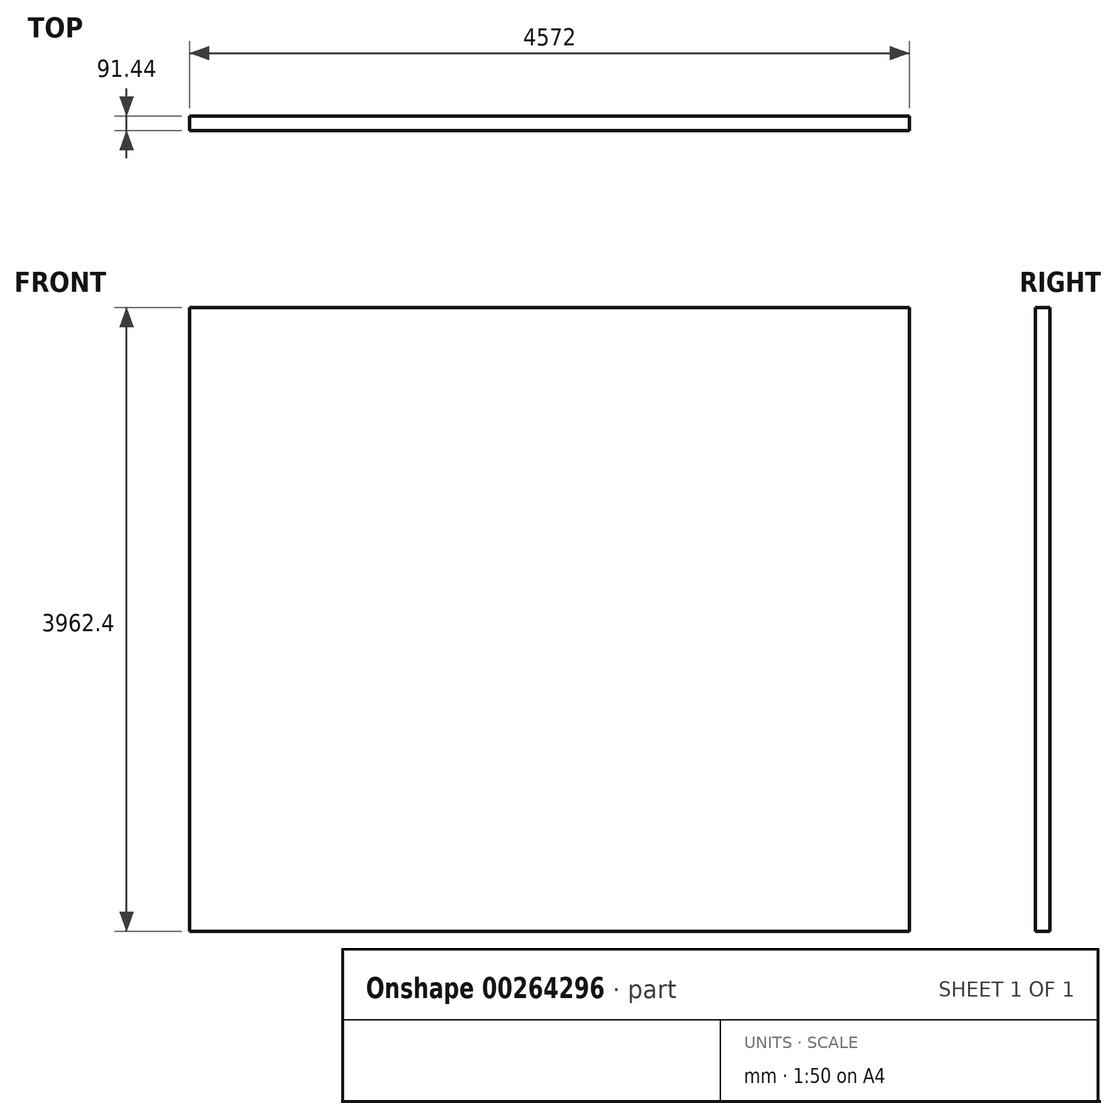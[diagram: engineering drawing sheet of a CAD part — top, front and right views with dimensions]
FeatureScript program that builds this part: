
annotation { "Feature Type Name" : "Feature", "Feature Type Description" : "" }
export const myFeature = defineFeature(function(context is Context, id is Id, definition is map)
    precondition{}
    {
        {
            var Q0;
            Q0=qCreatedBy(makeId("Top.planeOp"),FACE);
            var sketch = newSketch(context, id + "F0", { "sketchPlane" : qUnion([Q0])});
            skLineSegment(sketch, "E0.bottom", {"start": v(-2250.5, 103.97) * mm, "end": v(2321.5, 103.97) * mm});
            skLineSegment(sketch, "E0.top", {"start": v(-2250.5, 12.53) * mm, "end": v(2321.5, 12.53) * mm});
            skLineSegment(sketch, "E0.left", {"start": v(-2250.5, 103.97) * mm, "end": v(-2250.5, 12.53) * mm});
            skLineSegment(sketch, "E0.right", {"start": v(2321.5, 103.97) * mm, "end": v(2321.5, 12.53) * mm});
            skSolve(sketch);
        }
        {
            var Q0;
            Q0=makeQuery(id+"F0.imprint","IMPRINT",FACE,{"disambiguationData":[TD([[makeQuery(id+"F0.imprint","IMPRINT",EDGE,{"derivedFrom":sQuery(id+"F0.wireOp",EDGE,"E0.bottom")}),-1.0]])]});
            extrude(context, id + "F1", {"entities" : qUnion([Q0]), "depth" : 3962.4 * mm, "offsetDistance" : 30.48 * mm});
        }
    });
